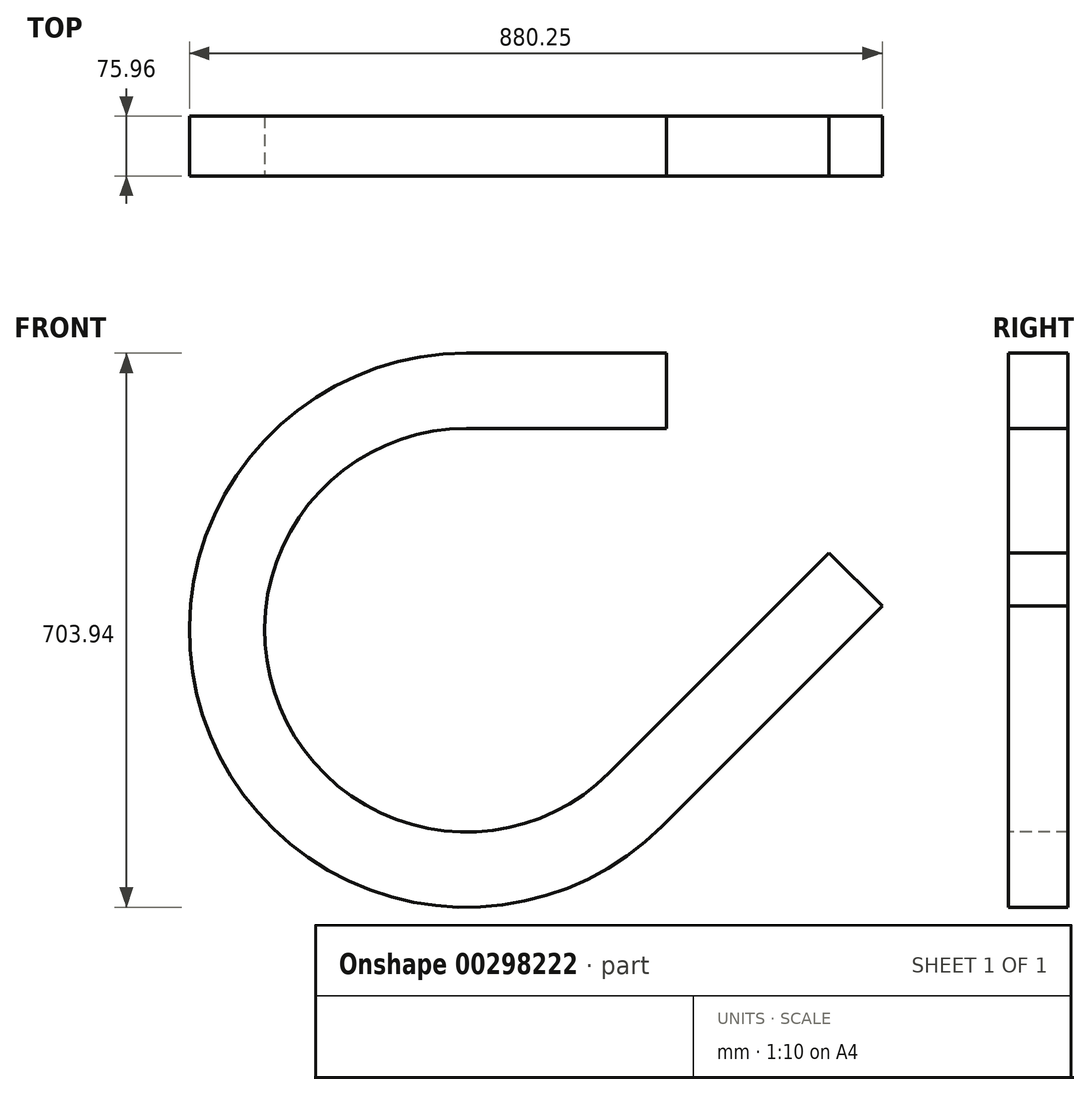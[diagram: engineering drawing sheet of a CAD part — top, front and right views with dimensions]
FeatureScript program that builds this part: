
annotation { "Feature Type Name" : "Feature", "Feature Type Description" : "" }
export const myFeature = defineFeature(function(context is Context, id is Id, definition is map)
    precondition{}
    {
        {
            var Q0;
            Q0=qCreatedBy(makeId("Front.planeOp"),FACE);
            var sketch = newSketch(context, id + "F0", { "sketchPlane" : qUnion([Q0])});
            skArc(sketch, "E0", {"start": v(0, 304.8) * mm, "mid": v(-281.6, -116.64) * mm, "end": v(215.53, -215.53) * mm});
            skLineSegment(sketch, "E1", {"start": v(0, 304.8) * mm, "end": v(254, 304.8) * mm});
            skLineSegment(sketch, "E2", {"start": v(215.53, -215.53) * mm, "end": v(494.93, 63.87) * mm});
            skLineSegment(sketch, "E3", {"start": v(0, 0) * mm, "end": v(0, 157.51) * mm, "construction": true});
            skLineSegment(sketch, "E4", {"start": v(254, 304.8) * mm, "end": v(494.93, 63.87) * mm, "construction": true});
            skSolve(sketch);
        }
        {
            var Q0;
            Q0=sQuery(id+"F0.wireOp",VERTEX,"E4.start");
            var Q1;
            Q1=sQuery(id+"F0.wireOp",EDGE,"E1");
            cPlane(context, id + "F1", {"entities" : qUnion([Q0, Q1]), "cplaneType" : CPlaneType.LINE_POINT, "offset" : 25.4 * mm, "width" : 152.4 * mm, "height" : 152.4 * mm});
        }
        {
            var Q0;
            Q0=qCreatedBy(id+"F1.planeOp",FACE);
            var sketch = newSketch(context, id + "F2", { "sketchPlane" : qUnion([Q0])});
            skLineSegment(sketch, "E5.bottom", {"start": v(37.98, 351.97) * mm, "end": v(-37.98, 351.97) * mm});
            skLineSegment(sketch, "E5.top", {"start": v(37.98, 256.4) * mm, "end": v(-37.98, 256.4) * mm});
            skLineSegment(sketch, "E5.left", {"start": v(37.98, 351.97) * mm, "end": v(37.98, 256.4) * mm});
            skLineSegment(sketch, "E5.right", {"start": v(-37.98, 351.97) * mm, "end": v(-37.98, 256.4) * mm});
            skPoint(sketch, "E5.middle", {"position": v(0, 304.19) * mm});
            skLineSegment(sketch, "E6.0", {"start": v(44.33, 358.32) * mm, "end": v(-44.33, 358.32) * mm});
            skLineSegment(sketch, "E6.1", {"start": v(44.33, 358.32) * mm, "end": v(44.33, 250.06) * mm});
            skLineSegment(sketch, "E6.2", {"start": v(44.33, 250.06) * mm, "end": v(-44.33, 250.06) * mm});
            skLineSegment(sketch, "E6.3", {"start": v(-44.33, 358.32) * mm, "end": v(-44.33, 250.06) * mm});
            skSolve(sketch);
        }
        {
            var Q0;
            Q0=makeQuery(id+"F2.imprint","IMPRINT",FACE,{"disambiguationData":[TD([[makeQuery(id+"F2.imprint","IMPRINT",EDGE,{"derivedFrom":sQuery(id+"F2.wireOp",EDGE,"E5.bottom")}),1.0]])]});
            var Q1;
            Q1=sQuery(id+"F0.wireOp",EDGE,"E0");
            var Q2;
            Q2=sQuery(id+"F0.wireOp",EDGE,"E1");
            var Q3;
            Q3=sQuery(id+"F0.wireOp",EDGE,"E2");
            sweep(context, id + "F3", {"profiles" : qUnion([Q0]), "path" : qUnion([Q1, Q2, Q3])});
        }
    });
